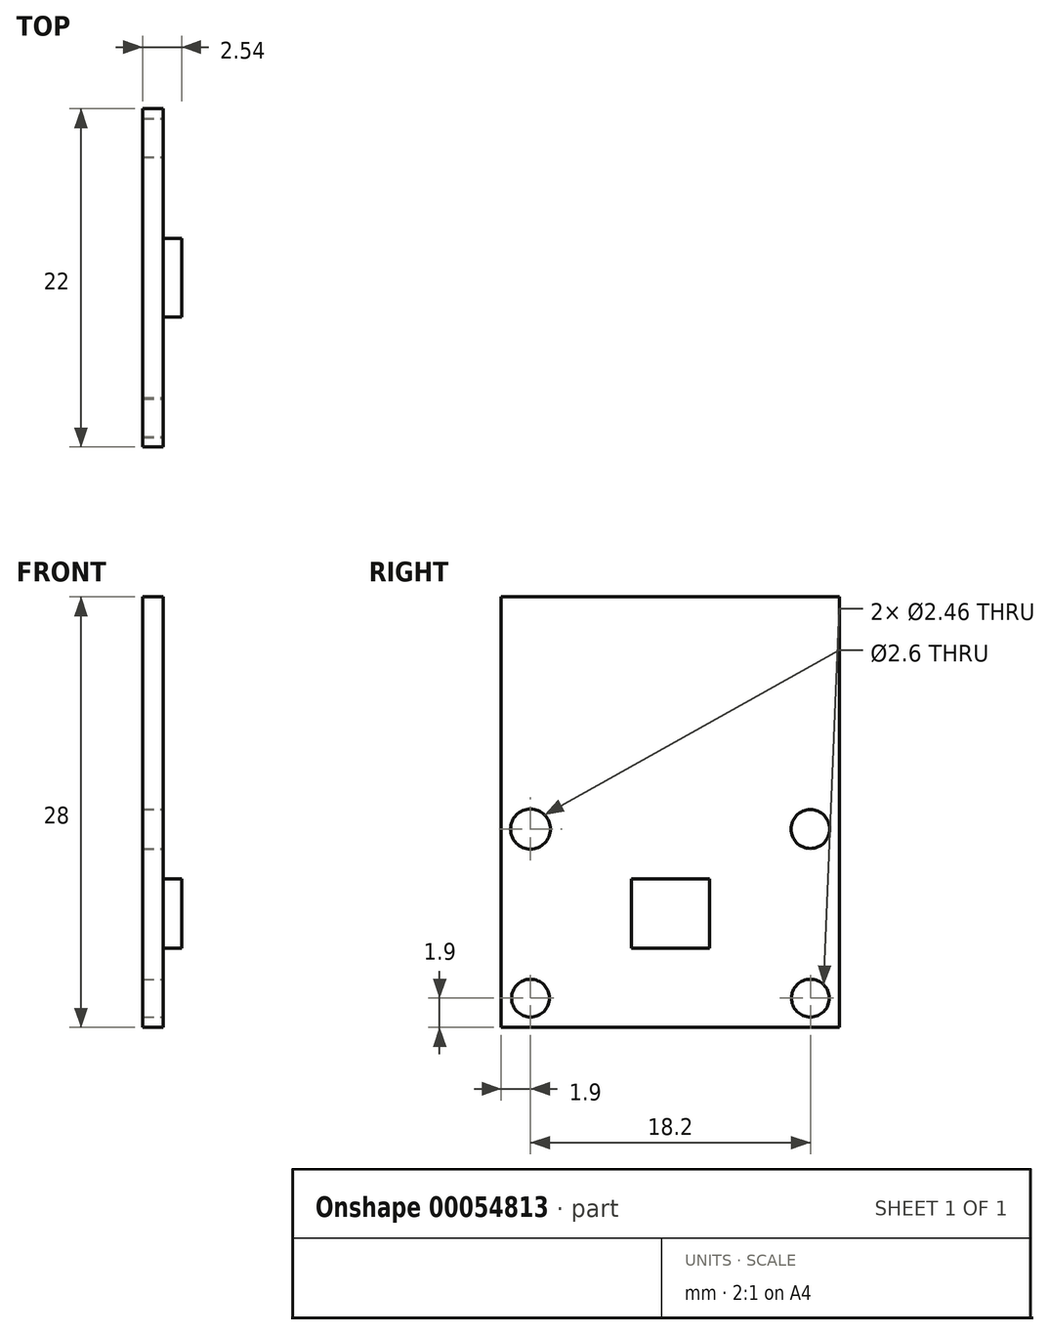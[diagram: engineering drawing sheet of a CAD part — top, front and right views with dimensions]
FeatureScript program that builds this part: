
annotation { "Feature Type Name" : "Feature", "Feature Type Description" : "" }
export const myFeature = defineFeature(function(context is Context, id is Id, definition is map)
    precondition{}
    {
        {
            var Q0;
            Q0=qCreatedBy(makeId("Right.planeOp"),FACE);
            var sketch = newSketch(context, id + "F0", { "sketchPlane" : qUnion([Q0])});
            skLineSegment(sketch, "E0.rect.bottom", {"start": v(11, 14) * mm, "end": v(-11, 14) * mm});
            skLineSegment(sketch, "E0.rect.top", {"start": v(11, -14) * mm, "end": v(-11, -14) * mm});
            skLineSegment(sketch, "E0.rect.left", {"start": v(11, 14) * mm, "end": v(11, -14) * mm});
            skLineSegment(sketch, "E0.rect.right", {"start": v(-11, 14) * mm, "end": v(-11, -14) * mm});
            skPoint(sketch, "E0.rect.middle", {"position": v(0, 0) * mm});
            skLineSegment(sketch, "E1.bottom", {"start": v(-9.1, -1.1) * mm, "end": v(9.1, -1.1) * mm, "construction": true});
            skLineSegment(sketch, "E1.top", {"start": v(-9.1, -12.1) * mm, "end": v(9.1, -12.1) * mm, "construction": true});
            skLineSegment(sketch, "E1.left", {"start": v(-9.1, -1.1) * mm, "end": v(-9.1, -12.1) * mm, "construction": true});
            skLineSegment(sketch, "E1.right", {"start": v(9.1, -1.1) * mm, "end": v(9.1, -12.1) * mm, "construction": true});
            skCircle(sketch, "E2", {"center": v(-9.1, -1.1) * mm, "radius": 1.3 * mm});
            skCircle(sketch, "E3", {"center": v(9.1, -1.1) * mm, "radius": 1.26 * mm});
            skCircle(sketch, "E4", {"center": v(9.1, -12.1) * mm, "radius": 1.23 * mm});
            skCircle(sketch, "E5", {"center": v(-9.1, -12.1) * mm, "radius": 1.23 * mm});
            skLineSegment(sketch, "E6.rect.bottom", {"start": v(-2.55, -4.35) * mm, "end": v(2.55, -4.35) * mm});
            skLineSegment(sketch, "E6.rect.top", {"start": v(-2.55, -8.85) * mm, "end": v(2.55, -8.85) * mm});
            skLineSegment(sketch, "E6.rect.left", {"start": v(-2.55, -4.35) * mm, "end": v(-2.55, -8.85) * mm});
            skLineSegment(sketch, "E6.rect.right", {"start": v(2.55, -4.35) * mm, "end": v(2.55, -8.85) * mm});
            skPoint(sketch, "E6.rect.middle", {"position": v(0, -6.6) * mm});
            skSolve(sketch);
        }
        {
            var Q0;
            Q0=makeQuery(id+"F0.imprint","IMPRINT",FACE,{"disambiguationData":[TD([[makeQuery(id+"F0.imprint","IMPRINT",EDGE,{"derivedFrom":sQuery(id+"F0.wireOp",EDGE,"E0.rect.bottom")}),1.0]])]});
            var Q1;
            Q1=makeQuery(id+"F0.imprint","IMPRINT",FACE,{"disambiguationData":[TD([[makeQuery(id+"F0.imprint","IMPRINT",EDGE,{"derivedFrom":sQuery(id+"F0.wireOp",EDGE,"E6.rect.bottom")}),-1.0]])]});
            var Q2;
            Q2=sQuery(id+"F0.wireOp",EDGE,"E0.rect.top");
            extrude(context, id + "F1", {"entities" : qUnion([Q0, Q1]), "surfaceEntities" : qUnion([Q2]), "oppositeDirection" : true, "depth" : 2.54 * mm - 1.2 * mm});
        }
        {
            var Q0;
            Q0=makeQuery(id+"F0.imprint","IMPRINT",FACE,{"disambiguationData":[TD([[makeQuery(id+"F0.imprint","IMPRINT",EDGE,{"derivedFrom":sQuery(id+"F0.wireOp",EDGE,"E6.rect.bottom")}),-1.0]])]});
            extrude(context, id + "F2", {"entities" : qUnion([Q0]), "depth" : 1.2 * mm});
        }
    });
